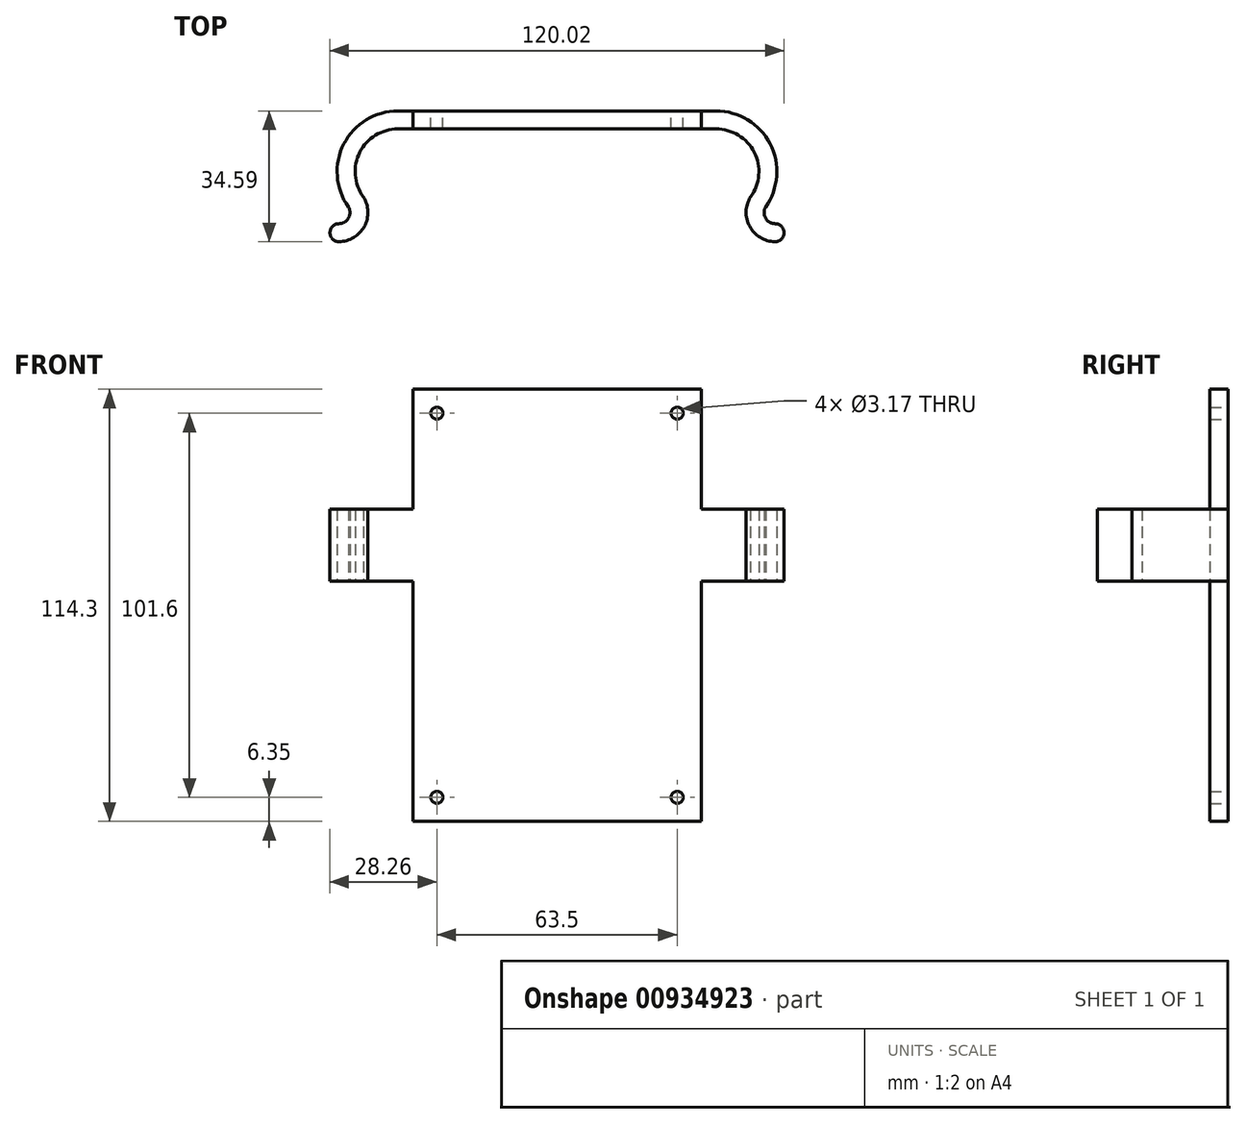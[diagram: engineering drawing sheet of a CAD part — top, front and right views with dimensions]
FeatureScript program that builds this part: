
annotation { "Feature Type Name" : "Feature", "Feature Type Description" : "" }
export const myFeature = defineFeature(function(context is Context, id is Id, definition is map)
    precondition{}
    {
        {
            var Q0;
            Q0=qCreatedBy(makeId("Top.planeOp"),FACE);
            var sketch = newSketch(context, id + "F0", { "sketchPlane" : qUnion([Q0])});
            skArc(sketch, "E0", {"start": v(51.15, -6.68) * mm, "mid": v(52.12, 5.11) * mm, "end": v(42.04, 11.3) * mm});
            skLineSegment(sketch, "E1", {"start": v(42.04, 11.3) * mm, "end": v(0, 11.3) * mm});
            skArc(sketch, "E2", {"start": v(55.12, -9.32) * mm, "mid": v(56.32, 7.36) * mm, "end": v(42.04, 16.07) * mm});
            skLineSegment(sketch, "E3", {"start": v(42.04, 16.07) * mm, "end": v(0, 16.07) * mm});
            skArc(sketch, "E4", {"start": v(51.15, -6.68) * mm, "mid": v(50.92, -14.53) * mm, "end": v(57.68, -18.52) * mm});
            skArc(sketch, "E5", {"start": v(55.12, -9.32) * mm, "mid": v(55.12, -12.28) * mm, "end": v(57.68, -13.76) * mm});
            skArc(sketch, "E6", {"start": v(57.6, -18.52) * mm, "mid": v(60, -16.16) * mm, "end": v(57.65, -13.76) * mm});
            skLineSegment(sketch, "E7", {"start": v(0, 0) * mm, "end": v(0, 27.63) * mm, "construction": true});
            skLineSegment(sketch, "E8.MirrorCS", {"start": v(-42.04, 11.3) * mm, "end": v(0, 11.3) * mm});
            skLineSegment(sketch, "E9.MirrorCS", {"start": v(-42.04, 16.07) * mm, "end": v(0, 16.07) * mm});
            skArc(sketch, "E10.MirrorCS", {"start": v(-55.12, -9.32) * mm, "mid": v(-56.32, 7.36) * mm, "end": v(-42.04, 16.07) * mm});
            skArc(sketch, "E11.MirrorCS", {"start": v(-51.15, -6.68) * mm, "mid": v(-52.12, 5.11) * mm, "end": v(-42.04, 11.3) * mm});
            skArc(sketch, "E12.MirrorCS", {"start": v(-51.15, -6.68) * mm, "mid": v(-50.92, -14.53) * mm, "end": v(-57.68, -18.52) * mm});
            skArc(sketch, "E13.MirrorCS", {"start": v(-55.12, -9.32) * mm, "mid": v(-55.12, -12.28) * mm, "end": v(-57.68, -13.76) * mm});
            skArc(sketch, "E14.MirrorCS", {"start": v(-57.6, -18.52) * mm, "mid": v(-60, -16.16) * mm, "end": v(-57.65, -13.76) * mm});
            skSolve(sketch);
        }
        {
            var Q0;
            Q0 = qSketchRegion(id + "F0", true);
            extrude(context, id + "F1", {"entities" : qUnion([Q0]), "depth" : 19.05 * mm, "offsetDistance" : 25.4 * mm});
        }
        {
            var Q0;
            Q0=makeQuery(id+"F1.opExtrude","SWEPT_FACE",FACE,{"disambiguationData":[OSD([sQuery(id+"F0.wireOp",EDGE,"E3"),sQuery(id+"F0.wireOp",EDGE,"E9.MirrorCS")])]});
            var sketch = newSketch(context, id + "F2", { "sketchPlane" : qUnion([Q0])});
            skLineSegment(sketch, "E15", {"start": v(-38.1, 19.05) * mm, "end": v(-38.1, 50.8) * mm});
            skLineSegment(sketch, "E16", {"start": v(-38.1, 50.8) * mm, "end": v(38.1, 50.8) * mm});
            skLineSegment(sketch, "E17", {"start": v(38.1, 50.8) * mm, "end": v(38.1, 19.05) * mm});
            skLineSegment(sketch, "E18", {"start": v(-38.1, 0) * mm, "end": v(-38.1, -63.5) * mm});
            skLineSegment(sketch, "E19", {"start": v(-38.1, -63.5) * mm, "end": v(38.1, -63.5) * mm});
            skLineSegment(sketch, "E20", {"start": v(38.1, -63.5) * mm, "end": v(38.1, 0) * mm});
            skLineSegment(sketch, "E21", {"start": v(0, 50.8) * mm, "end": v(0, 55.61) * mm, "construction": true});
            skPoint(sketch, "E21.startSnap0", {"position": v(0, 0) * mm});
            skLineSegment(sketch, "E22", {"start": v(-38.1, 19.05) * mm, "end": v(38.1, 19.05) * mm});
            skLineSegment(sketch, "E23", {"start": v(38.1, 0) * mm, "end": v(-38.1, 0) * mm});
            skSolve(sketch);
        }
        {
            var Q0;
            Q0 = qSketchRegion(id + "F2", true);
            extrude(context, id + "F3", {"entities" : qUnion([Q0]), "operationType" : NewBodyOperationType.ADD, "oppositeDirection" : true, "depth" : 4.76 * mm, "offsetDistance" : 25.4 * mm});
        }
        {
            var Q0;
            Q0=makeQuery(id+"F3.boolean.opBoolean","MERGE",FACE,{"derivedFrom":[makeQuery(id+"F1.opExtrude","SWEPT_FACE",FACE,{"disambiguationData":[OSD([sQuery(id+"F0.wireOp",EDGE,"E3"),sQuery(id+"F0.wireOp",EDGE,"E9.MirrorCS")])]}),makeQuery(id+"F3.opExtrude","CAP_FACE",FACE,{"disambiguationData":[OSD([sQuery(id+"F2.wireOp",EDGE,"E15"),sQuery(id+"F2.wireOp",EDGE,"E16"),sQuery(id+"F2.wireOp",EDGE,"E17"),sQuery(id+"F2.wireOp",EDGE,"E22")])],"isStart":true}),makeQuery(id+"F3.opExtrude","CAP_FACE",FACE,{"disambiguationData":[OSD([sQuery(id+"F2.wireOp",EDGE,"E18"),sQuery(id+"F2.wireOp",EDGE,"E19"),sQuery(id+"F2.wireOp",EDGE,"E20"),sQuery(id+"F2.wireOp",EDGE,"E23")])],"isStart":true})]});
            var sketch = newSketch(context, id + "F4", { "sketchPlane" : qUnion([Q0])});
            skCircle(sketch, "E24", {"center": v(-31.75, 44.45) * mm, "radius": 1.59 * mm});
            skCircle(sketch, "E25", {"center": v(31.75, 44.45) * mm, "radius": 1.59 * mm});
            skCircle(sketch, "E26", {"center": v(31.75, -57.15) * mm, "radius": 1.59 * mm});
            skCircle(sketch, "E27", {"center": v(-31.75, -57.15) * mm, "radius": 1.59 * mm});
            skSolve(sketch);
        }
        {
            var Q0;
            Q0 = qSketchRegion(id + "F4", true);
            extrude(context, id + "F5", {"entities" : qUnion([Q0]), "operationType" : NewBodyOperationType.REMOVE, "oppositeDirection" : true, "depth" : 4.76 * mm, "offsetDistance" : 25.4 * mm});
        }
    });
